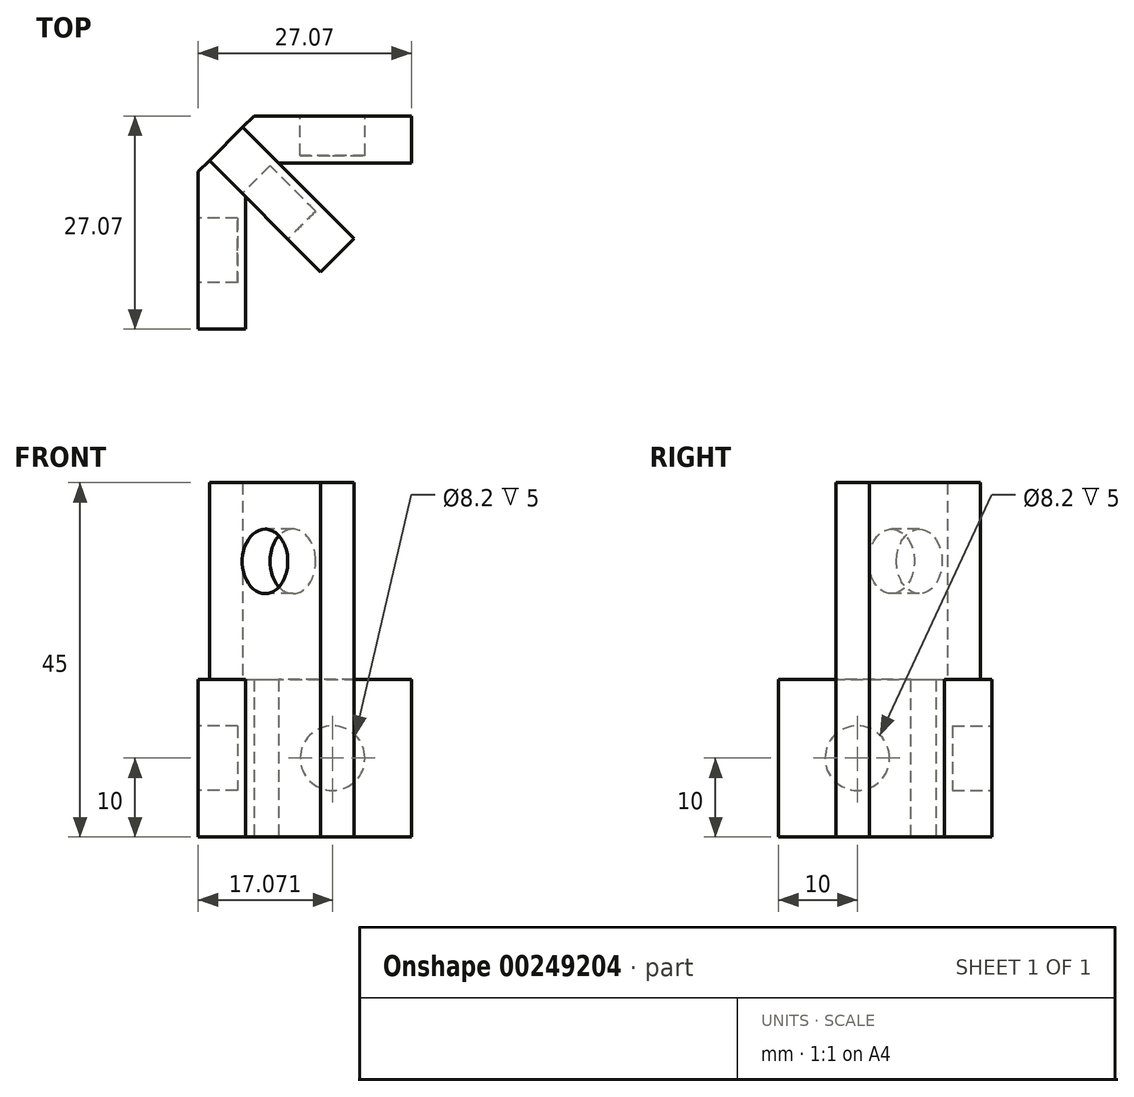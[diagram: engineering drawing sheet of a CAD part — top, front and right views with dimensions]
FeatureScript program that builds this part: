
annotation { "Feature Type Name" : "Feature", "Feature Type Description" : "" }
export const myFeature = defineFeature(function(context is Context, id is Id, definition is map)
    precondition{}
    {
        {
            var Q0;
            Q0=qCreatedBy(makeId("Top.planeOp"),FACE);
            var sketch = newSketch(context, id + "F0", { "sketchPlane" : qUnion([Q0])});
            skLineSegment(sketch, "E0", {"start": v(0, 0) * mm, "end": v(7.07, 7.07) * mm});
            skLineSegment(sketch, "E1", {"start": v(7.07, 7.07) * mm, "end": v(27.07, 7.07) * mm});
            skLineSegment(sketch, "E2", {"start": v(27.07, 7.07) * mm, "end": v(27.07, 1.07) * mm});
            skLineSegment(sketch, "E3", {"start": v(27.07, 1.07) * mm, "end": v(9.56, 1.07) * mm});
            skLineSegment(sketch, "E4", {"start": v(9.56, 1.07) * mm, "end": v(6, -2.49) * mm});
            skLineSegment(sketch, "E5", {"start": v(6, -2.49) * mm, "end": v(6, -20) * mm});
            skLineSegment(sketch, "E6", {"start": v(6, -20) * mm, "end": v(0, -20) * mm});
            skLineSegment(sketch, "E7", {"start": v(0, -20) * mm, "end": v(0, 0) * mm});
            skSolve(sketch);
        }
        {
            var Q0;
            Q0 = qSketchRegion(id + "F0", true);
            extrude(context, id + "F1", {"entities" : qUnion([Q0]), "depth" : 20 * mm});
        }
        {
            var Q0;
            Q0=makeQuery(id+"F1.opExtrude","CAP_FACE",FACE,{"disambiguationData":[OSD([sQuery(id+"F0.wireOp",EDGE,"E0"),sQuery(id+"F0.wireOp",EDGE,"E1"),sQuery(id+"F0.wireOp",EDGE,"E2"),sQuery(id+"F0.wireOp",EDGE,"E3"),sQuery(id+"F0.wireOp",EDGE,"E4"),sQuery(id+"F0.wireOp",EDGE,"E5"),sQuery(id+"F0.wireOp",EDGE,"E6"),sQuery(id+"F0.wireOp",EDGE,"E7")])],"isStart":false});
            var sketch = newSketch(context, id + "F2", { "sketchPlane" : qUnion([Q0])});
            skLineSegment(sketch, "E8", {"start": v(3.54, 3.54) * mm, "end": v(17.68, -10.6) * mm});
            skLineSegment(sketch, "E9", {"start": v(17.68, -10.6) * mm, "end": v(19.8, -8.49) * mm});
            skLineSegment(sketch, "E10", {"start": v(19.8, -8.49) * mm, "end": v(5.66, 5.66) * mm});
            skLineSegment(sketch, "E11", {"start": v(5.66, 5.66) * mm, "end": v(1.41, 1.41) * mm});
            skLineSegment(sketch, "E12", {"start": v(1.41, 1.41) * mm, "end": v(15.56, -12.73) * mm});
            skLineSegment(sketch, "E13", {"start": v(17.68, -10.6) * mm, "end": v(15.56, -12.73) * mm});
            skSolve(sketch);
        }
        {
            var Q0;
            Q0 = qSketchRegion(id + "F2", true);
            extrude(context, id + "F3", {"entities" : qUnion([Q0]), "operationType" : NewBodyOperationType.ADD, "depth" : 25 * mm, "hasSecondDirection" : true, "secondDirectionOppositeDirection" : true, "secondDirectionDepth" : 20 * mm});
        }
        {
            var Q0;
            Q0=makeQuery(id+"F1.opExtrude","SWEPT_FACE",FACE,{"disambiguationData":[OSD([sQuery(id+"F0.wireOp",EDGE,"E7")])]});
            var sketch = newSketch(context, id + "F4", { "sketchPlane" : qUnion([Q0])});
            skCircle(sketch, "E14", {"center": v(10, 10) * mm, "radius": 4.1 * mm});
            skPoint(sketch, "E14.centerSnap0", {"position": v(20, 10) * mm});
            skPoint(sketch, "E14.centerSnap1", {"position": v(10, 20) * mm});
            skSolve(sketch);
        }
        {
            var Q0;
            Q0 = qSketchRegion(id + "F4", true);
            extrude(context, id + "F5", {"entities" : qUnion([Q0]), "operationType" : NewBodyOperationType.REMOVE, "oppositeDirection" : true, "depth" : 5 * mm});
        }
        {
            var Q0;
            Q0=makeQuery(id+"F1.opExtrude","SWEPT_FACE",FACE,{"disambiguationData":[OSD([sQuery(id+"F0.wireOp",EDGE,"E1")])]});
            var sketch = newSketch(context, id + "F6", { "sketchPlane" : qUnion([Q0])});
            skCircle(sketch, "E15", {"center": v(-17.07, 10) * mm, "radius": 4.1 * mm});
            skPoint(sketch, "E15.centerSnap0", {"position": v(-17.07, 20) * mm});
            skPoint(sketch, "E15.centerSnap1", {"position": v(-27.07, 10) * mm});
            skSolve(sketch);
        }
        {
            var Q0;
            Q0 = qSketchRegion(id + "F6", true);
            extrude(context, id + "F7", {"entities" : qUnion([Q0]), "operationType" : NewBodyOperationType.REMOVE, "oppositeDirection" : true, "depth" : 5 * mm});
        }
        {
            var Q0;
            Q0=makeQuery(id+"F3.opExtrude","SWEPT_FACE",FACE,{"disambiguationData":[OSD([sQuery(id+"F2.wireOp",EDGE,"E12")])]});
            var sketch = newSketch(context, id + "F8", { "sketchPlane" : qUnion([Q0])});
            skCircle(sketch, "E16", {"center": v(10, 35) * mm, "radius": 4.1 * mm});
            skPoint(sketch, "E16.centerSnap0", {"position": v(10, 45) * mm});
            skSolve(sketch);
        }
        {
            var Q0;
            Q0 = qSketchRegion(id + "F8", true);
            extrude(context, id + "F9", {"entities" : qUnion([Q0]), "operationType" : NewBodyOperationType.REMOVE, "oppositeDirection" : true, "depth" : 5 * mm});
        }
    });
